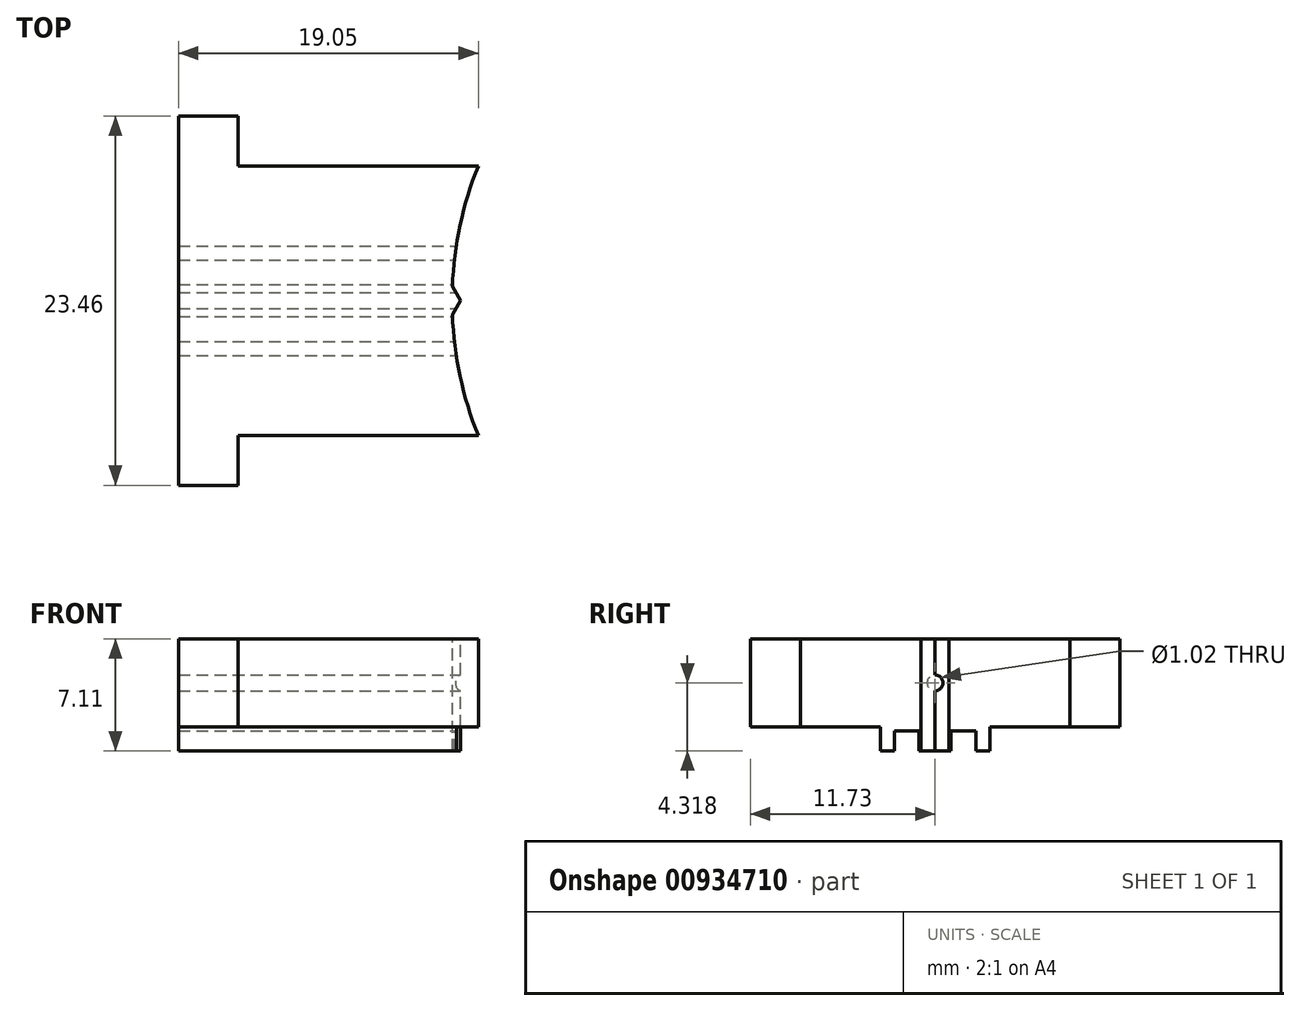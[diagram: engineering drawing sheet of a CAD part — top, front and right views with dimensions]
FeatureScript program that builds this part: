
annotation { "Feature Type Name" : "Feature", "Feature Type Description" : "" }
export const myFeature = defineFeature(function(context is Context, id is Id, definition is map)
    precondition{}
    {
        {
            var Q0;
            Q0=qCreatedBy(makeId("Right.planeOp"),FACE);
            var sketch = newSketch(context, id + "F0", { "sketchPlane" : qUnion([Q0])});
            skLineSegment(sketch, "E0.bottom", {"start": v(-1.02, 0) * mm, "end": v(1.02, 0) * mm});
            skLineSegment(sketch, "E0.left", {"start": v(-1.02, 0) * mm, "end": v(-1.02, 1.27) * mm});
            skLineSegment(sketch, "E0.right", {"start": v(1.02, 0) * mm, "end": v(1.02, 1.27) * mm});
            skLineSegment(sketch, "E1.left", {"start": v(2.6, 0) * mm, "end": v(2.6, 1.27) * mm});
            skLineSegment(sketch, "E2.left", {"start": v(-2.6, 0) * mm, "end": v(-2.6, 1.27) * mm});
            skLineSegment(sketch, "E3", {"start": v(0, 7.11) * mm, "end": v(0, 0) * mm, "construction": true});
            skLineSegment(sketch, "E4", {"start": v(-8.56, 7.11) * mm, "end": v(8.56, 7.11) * mm});
            skLineSegment(sketch, "E5", {"start": v(-2.6, 1.27) * mm, "end": v(-1.02, 1.27) * mm});
            skLineSegment(sketch, "E6", {"start": v(1.02, 1.27) * mm, "end": v(2.6, 1.27) * mm});
            skLineSegment(sketch, "E7", {"start": v(-3.48, 1.52) * mm, "end": v(-3.48, 0) * mm});
            skLineSegment(sketch, "E8", {"start": v(3.48, 1.52) * mm, "end": v(3.48, 0) * mm});
            skLineSegment(sketch, "E9", {"start": v(-2.6, 0) * mm, "end": v(-3.48, 0) * mm});
            skLineSegment(sketch, "E10", {"start": v(3.48, 0) * mm, "end": v(2.6, 0) * mm});
            skLineSegment(sketch, "E11", {"start": v(-8.56, 1.52) * mm, "end": v(-3.48, 1.52) * mm});
            skLineSegment(sketch, "E12", {"start": v(3.48, 1.52) * mm, "end": v(8.56, 1.52) * mm});
            skLineSegment(sketch, "E13", {"start": v(-8.56, 7.11) * mm, "end": v(-8.56, 1.52) * mm});
            skLineSegment(sketch, "E14", {"start": v(8.56, 7.11) * mm, "end": v(8.56, 1.52) * mm});
            skSolve(sketch);
        }
        {
            var Q0;
            Q0 = qSketchRegion(id + "F0", true);
            extrude(context, id + "F1", {"entities" : qUnion([Q0]), "oppositeDirection" : true, "depth" : 19.05 * mm, "offsetDistance" : 25.4 * mm});
        }
        {
            var Q0;
            Q0=makeQuery(id+"F1.opExtrude","SWEPT_FACE",FACE,{"disambiguationData":[OSD([sQuery(id+"F0.wireOp",EDGE,"E4")])]});
            var sketch = newSketch(context, id + "F2", { "sketchPlane" : qUnion([Q0])});
            skPoint(sketch, "E15.oppositeSnap0", {"position": v(-15.24, -8.56) * mm});
            skLineSegment(sketch, "E15.bottom", {"start": v(-19.05, 8.56) * mm, "end": v(-15.24, 8.56) * mm});
            skLineSegment(sketch, "E15.top", {"start": v(-19.05, 11.73) * mm, "end": v(-15.24, 11.73) * mm});
            skLineSegment(sketch, "E15.left", {"start": v(-19.05, 8.56) * mm, "end": v(-19.05, 11.73) * mm});
            skLineSegment(sketch, "E15.right", {"start": v(-15.24, 8.56) * mm, "end": v(-15.24, 11.73) * mm});
            skLineSegment(sketch, "E16.MirrorCS", {"start": v(-19.05, -8.56) * mm, "end": v(-19.05, -11.73) * mm});
            skLineSegment(sketch, "E17.MirrorCS", {"start": v(-19.05, -8.56) * mm, "end": v(-15.24, -8.56) * mm});
            skLineSegment(sketch, "E18.MirrorCS", {"start": v(-15.24, -8.56) * mm, "end": v(-15.24, -11.73) * mm});
            skLineSegment(sketch, "E19.MirrorCS", {"start": v(-19.05, -11.73) * mm, "end": v(-15.24, -11.73) * mm});
            skSolve(sketch);
        }
        {
            var Q0;
            Q0 = qSketchRegion(id + "F2", true);
            var Q1;
            Q1=makeQuery(id+"F1.opExtrude","SWEPT_FACE",FACE,{"disambiguationData":[OSD([sQuery(id+"F0.wireOp",EDGE,"E12")])]});
            extrude(context, id + "F3", {"entities" : qUnion([Q0]), "operationType" : NewBodyOperationType.ADD, "endBound" : BoundingType.UP_TO_SURFACE, "oppositeDirection" : true, "depth" : 25.4 * mm, "endBoundEntityFace" : qUnion([Q1]), "offsetDistance" : 25.4 * mm});
        }
        {
            var Q0;
            Q0=makeQuery(id+"F3.boolean.opBoolean","MERGE",FACE,{"derivedFrom":[makeQuery(id+"F1.opExtrude","SWEPT_FACE",FACE,{"disambiguationData":[OSD([sQuery(id+"F0.wireOp",EDGE,"E4")])]}),makeQuery(id+"F3.opExtrude","CAP_FACE",FACE,{"disambiguationData":[OSD([sQuery(id+"F2.wireOp",EDGE,"E15.bottom"),sQuery(id+"F2.wireOp",EDGE,"E15.top"),sQuery(id+"F2.wireOp",EDGE,"E15.left"),sQuery(id+"F2.wireOp",EDGE,"E15.right")])],"isStart":true}),makeQuery(id+"F3.opExtrude","CAP_FACE",FACE,{"disambiguationData":[OSD([sQuery(id+"F2.wireOp",EDGE,"E16.MirrorCS"),sQuery(id+"F2.wireOp",EDGE,"E17.MirrorCS"),sQuery(id+"F2.wireOp",EDGE,"E18.MirrorCS"),sQuery(id+"F2.wireOp",EDGE,"E19.MirrorCS")])],"isStart":true})]});
            var sketch = newSketch(context, id + "F4", { "sketchPlane" : qUnion([Q0])});
            skArc(sketch, "E20", {"start": v(0, 8.56) * mm, "mid": v(-1.15, 4.8) * mm, "end": v(-1.65, 0.89) * mm});
            skLineSegment(sketch, "E21", {"start": v(0, 8.56) * mm, "end": v(0, -8.56) * mm});
            skLineSegment(sketch, "E22", {"start": v(-1.65, -0.89) * mm, "end": v(-1.14, 0) * mm});
            skPoint(sketch, "E23.endSnap0", {"position": v(-1.66, 0) * mm});
            skLineSegment(sketch, "E24", {"start": v(-1.14, 0) * mm, "end": v(-1.65, 0.89) * mm});
            skLineSegment(sketch, "E25", {"start": v(-1.65, 0.89) * mm, "end": v(-1.65, -0.89) * mm, "construction": true});
            skLineSegment(sketch, "E26", {"start": v(-1.65, 0) * mm, "end": v(-1.14, 0) * mm, "construction": true});
            skArc(sketch, "E27", {"start": v(-1.65, -0.89) * mm, "mid": v(-1.15, -4.8) * mm, "end": v(0, -8.56) * mm});
            skSolve(sketch);
        }
        {
            var Q0;
            Q0 = qSketchRegion(id + "F4", true);
            extrude(context, id + "F5", {"entities" : qUnion([Q0]), "operationType" : NewBodyOperationType.REMOVE, "endBound" : BoundingType.THROUGH_ALL, "oppositeDirection" : true, "depth" : 25.4 * mm, "offsetDistance" : 25.4 * mm});
        }
        {
            var Q0;
            Q0=qCreatedBy(makeId("Right.planeOp"),FACE);
            var sketch = newSketch(context, id + "F6", { "sketchPlane" : qUnion([Q0])});
            skCircle(sketch, "E28", {"center": v(0, 4.32) * mm, "radius": 0.5 * mm});
            skLineSegment(sketch, "E29.0", {"start": v(-8.56, 7.11) * mm, "end": v(-8.56, 1.52) * mm});
            skLineSegment(sketch, "E30", {"start": v(-8.56, 4.32) * mm, "end": v(0, 4.32) * mm, "construction": true});
            skSolve(sketch);
        }
        {
            var Q0;
            Q0 = qSketchRegion(id + "F6", true);
            extrude(context, id + "F7", {"entities" : qUnion([Q0]), "operationType" : NewBodyOperationType.REMOVE, "endBound" : BoundingType.THROUGH_ALL, "oppositeDirection" : true, "depth" : 25.4 * mm, "offsetDistance" : 25.4 * mm});
        }
    });
